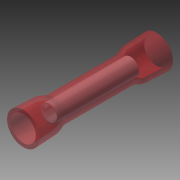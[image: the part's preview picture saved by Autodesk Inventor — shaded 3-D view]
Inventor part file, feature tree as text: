
AUTODESK INVENTOR PART (.ipt)
format: ipt  version: 2014 (Build 180170000, 170)  size: 181,760 bytes
history: native  units: in
note: dims shown in document units (in); Inventor stores cm internally (conversion verified against a paired STEP export)
features: extrude x2, sketch x2, fillet x1, mirror x1, shell x1, revolve x1, chamfer x1, projected_geometry x1
ambient origin geometry x8: Origin, YZ Plane, XZ Plane, XY Plane, X Axis, Y Axis, Z Axis, Center Point
bodies: Solid1 (feature_tree), Solid2 (feature_tree)
feature tree (10):
  extrude  "Extrusion1"  Depth=0.544in TaperAngle=0.0deg
  extrude  "Extrusion3"  Depth=0.1in
  fillet  "Fillet3"  [1 undecoded]
  mirror  "Mirror2"
  shell  "Shell1"  Thickness=0.008in
  revolve  "Revolution1"  [1 undecoded]
  chamfer  "Chamfer1"  Distance=0.0172in
  sketch  "Sketch1"  dims[d0=0.175in d1=0.544in d2=0.0in]
  sketch  "Sketch4"  dims[d8=0.0265in d9=0.0145in d12=90.0deg d13=0.008in d14=0.125in d15=45.0deg d16=0.215in d17=0.207in d18=0.0172in d19=0.1in]
  projected_geometry  "Project Cut Edges1"
note: 2 required parameter values undecoded (feature->parameter linkage not recoverable at this tier; creation-order binding heuristic only, values carry confidence <= 0.55)